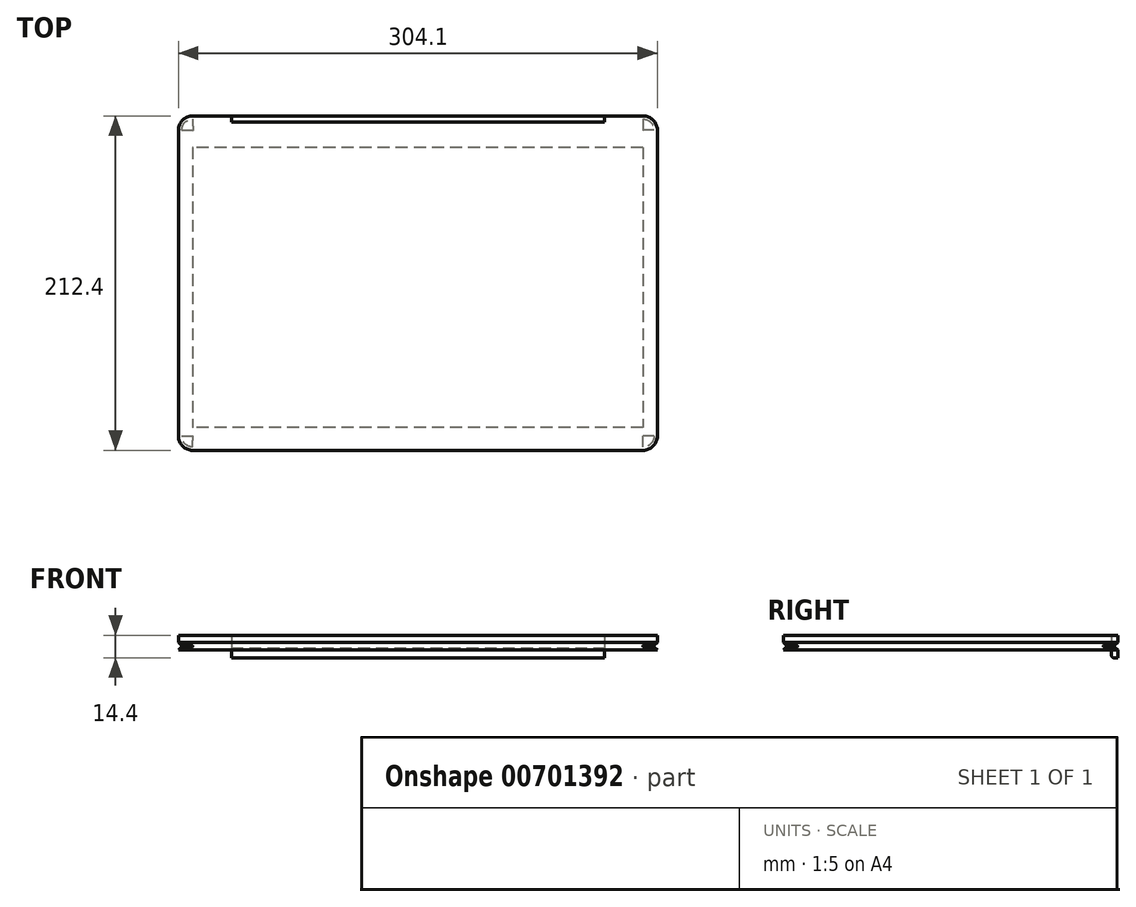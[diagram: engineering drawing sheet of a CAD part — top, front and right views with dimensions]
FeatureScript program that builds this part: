
annotation { "Feature Type Name" : "Feature", "Feature Type Description" : "" }
export const myFeature = defineFeature(function(context is Context, id is Id, definition is map)
    precondition{}
    {
        {
            assignVariable(context, id + "F0", {"name" : "swivel_depth", "anyValue" : 3 * mm});
        }
        {
            var Q0;
            Q0=qCreatedBy(makeId("Top.planeOp"),FACE);
            var sketch = newSketch(context, id + "F1", { "sketchPlane" : qUnion([Q0])});
            skLineSegment(sketch, "E0.bottom", {"start": v(143.05, -106.2) * mm, "end": v(-143.05, -106.2) * mm});
            skLineSegment(sketch, "E0.top", {"start": v(143.05, 106.2) * mm, "end": v(-143.05, 106.2) * mm});
            skLineSegment(sketch, "E0.left", {"start": v(152.05, -97.2) * mm, "end": v(152.05, 97.2) * mm});
            skLineSegment(sketch, "E0.right", {"start": v(-152.05, -97.2) * mm, "end": v(-152.05, 97.2) * mm});
            skPoint(sketch, "E0.middle", {"position": v(0, 0) * mm});
            skPoint(sketch, "E1.visualSharp", {"position": v(152.05, 106.2) * mm});
            skArc(sketch, "E1.filletArc", {"start": v(152.05, 97.2) * mm, "mid": v(149.41, 103.56) * mm, "end": v(143.05, 106.2) * mm});
            skPoint(sketch, "E2.visualSharp", {"position": v(-152.05, 106.2) * mm});
            skArc(sketch, "E2.filletArc", {"start": v(-143.05, 106.2) * mm, "mid": v(-149.41, 103.56) * mm, "end": v(-152.05, 97.2) * mm});
            skPoint(sketch, "E3.visualSharp", {"position": v(-152.05, -106.2) * mm});
            skArc(sketch, "E3.filletArc", {"start": v(-152.05, -97.2) * mm, "mid": v(-149.41, -103.56) * mm, "end": v(-143.05, -106.2) * mm});
            skPoint(sketch, "E4.visualSharp", {"position": v(152.05, -106.2) * mm});
            skArc(sketch, "E4.filletArc", {"start": v(143.05, -106.2) * mm, "mid": v(149.41, -103.56) * mm, "end": v(152.05, -97.2) * mm});
            skLineSegment(sketch, "E5", {"start": v(-118.5, 102.2) * mm, "end": v(118.5, 102.2) * mm});
            skPoint(sketch, "E6", {"position": v(0, 102.2) * mm});
            skPoint(sketch, "E7", {"position": v(0, 106.2) * mm});
            skLineSegment(sketch, "E8", {"start": v(-118.5, 102.2) * mm, "end": v(-118.5, 106.2) * mm});
            skLineSegment(sketch, "E9", {"start": v(118.5, 102.2) * mm, "end": v(118.5, 106.2) * mm});
            skSolve(sketch);
        }
        {
            var Q0;
            Q0=makeQuery(id+"F1.imprint","IMPRINT",FACE,{"disambiguationData":[TD([[makeQuery(id+"F1.imprint","IMPRINT",EDGE,{"derivedFrom":sQuery(id+"F1.wireOp",EDGE,"E0.bottom")}),-1.0]])]});
            var Q1;
            Q1=makeQuery(id+"F1.imprint","IMPRINT",FACE,{"disambiguationData":[TD([[makeQuery(id+"F1.imprint","IMPRINT",EDGE,{"derivedFrom":sQuery(id+"F1.wireOp",EDGE,"E5")}),1.0]])]});
            extrude(context, id + "F2", {"entities" : qUnion([Q0, Q1]), "depth" : 9.4 * mm, "offsetDistance" : 25 * mm});
        }
        {
            var Q0;
            Q0=makeQuery(id+"F2.opExtrude","CAP_FACE",FACE,{"disambiguationData":[OSD([sQuery(id+"F1.wireOp",EDGE,"E0.bottom"),sQuery(id+"F1.wireOp",EDGE,"E0.top"),sQuery(id+"F1.wireOp",EDGE,"E0.left"),sQuery(id+"F1.wireOp",EDGE,"E0.right"),sQuery(id+"F1.wireOp",EDGE,"E1.filletArc"),sQuery(id+"F1.wireOp",EDGE,"E2.filletArc"),sQuery(id+"F1.wireOp",EDGE,"E3.filletArc"),sQuery(id+"F1.wireOp",EDGE,"E4.filletArc"),sQuery(id+"F1.wireOp",EDGE,"E5"),sQuery(id+"F1.wireOp",EDGE,"E8"),sQuery(id+"F1.wireOp",EDGE,"E9")])],"isStart":true});
            chamfer(context, id + "F3", {"entities" : qUnion([Q0]), "width" : 5 * mm, "tangentPropagation" : true});
        }
        {
            var Q0;
            Q0=makeQuery(id+"F2.opExtrude","CAP_FACE",FACE,{"disambiguationData":[OSD([sQuery(id+"F1.wireOp",EDGE,"E0.bottom"),sQuery(id+"F1.wireOp",EDGE,"E0.top"),sQuery(id+"F1.wireOp",EDGE,"E0.left"),sQuery(id+"F1.wireOp",EDGE,"E0.right"),sQuery(id+"F1.wireOp",EDGE,"E1.filletArc"),sQuery(id+"F1.wireOp",EDGE,"E2.filletArc"),sQuery(id+"F1.wireOp",EDGE,"E3.filletArc"),sQuery(id+"F1.wireOp",EDGE,"E4.filletArc"),sQuery(id+"F1.wireOp",EDGE,"E5"),sQuery(id+"F1.wireOp",EDGE,"E8"),sQuery(id+"F1.wireOp",EDGE,"E9")])],"isStart":true});
            fillet(context, id + "F4", {"entities" : qUnion([Q0]), "radius" : 10 * mm, "tangentPropagation" : true, "allowEdgeOverflow" : false});
        }
        {
            var Q0;
            Q0=makeQuery(id+"F1.imprint","IMPRINT",FACE,{"disambiguationData":[TD([[makeQuery(id+"F1.imprint","IMPRINT",EDGE,{"derivedFrom":sQuery(id+"F1.wireOp",EDGE,"E5")}),1.0]])]});
            extrude(context, id + "F5", {"entities" : qUnion([Q0]), "operationType" : NewBodyOperationType.REMOVE, "depth" : 25 * mm, "offsetDistance" : 25 * mm});
        }
        {
            var Q0;
            Q0=makeQuery(id+"F1.imprint","IMPRINT",FACE,{"disambiguationData":[TD([[makeQuery(id+"F1.imprint","IMPRINT",EDGE,{"derivedFrom":sQuery(id+"F1.wireOp",EDGE,"E0.bottom")}),-1.0]])]});
            var Q1;
            Q1=makeQuery(id+"F1.imprint","IMPRINT",FACE,{"disambiguationData":[TD([[makeQuery(id+"F1.imprint","IMPRINT",EDGE,{"derivedFrom":sQuery(id+"F1.wireOp",EDGE,"E5")}),1.0]])]});
            extrude(context, id + "F6", {"entities" : qUnion([Q0, Q1]), "depth" : 5 * mm, "offsetDistance" : 25 * mm});
        }
        {
            var Q0;
            Q0=makeQuery(id+"F1.imprint","IMPRINT",FACE,{"disambiguationData":[TD([[makeQuery(id+"F1.imprint","IMPRINT",EDGE,{"derivedFrom":sQuery(id+"F1.wireOp",EDGE,"E0.bottom")}),-1.0]])]});
            var sketch = newSketch(context, id + "F7", { "sketchPlane" : qUnion([Q0])});
            skLineSegment(sketch, "E10.bottom", {"start": v(143.05, 86.2) * mm, "end": v(-143.05, 86.2) * mm});
            skLineSegment(sketch, "E10.top", {"start": v(143.05, -91.8) * mm, "end": v(-143.05, -91.8) * mm});
            skLineSegment(sketch, "E10.left", {"start": v(143.05, 86.2) * mm, "end": v(143.05, -91.8) * mm});
            skLineSegment(sketch, "E10.right", {"start": v(-143.05, 86.2) * mm, "end": v(-143.05, -91.8) * mm});
            skPoint(sketch, "E10.middle", {"position": v(0, -2.8) * mm});
            skSolve(sketch);
        }
        {
            var Q0;
            Q0=makeQuery(id+"F7.imprint","IMPRINT",FACE,{"disambiguationData":[TD([[makeQuery(id+"F7.imprint","IMPRINT",EDGE,{"derivedFrom":sQuery(id+"F7.wireOp",EDGE,"E10.bottom")}),1.0]])]});
            extrude(context, id + "F8", {"entities" : qUnion([Q0]), "operationType" : NewBodyOperationType.REMOVE, "depth" : .25 * mm, "offsetDistance" : 25 * mm});
        }
        {
            var Q0;
            Q0=makeQuery(id+"F1.imprint","IMPRINT",FACE,{"disambiguationData":[TD([[makeQuery(id+"F1.imprint","IMPRINT",EDGE,{"derivedFrom":sQuery(id+"F1.wireOp",EDGE,"E5")}),1.0]])]});
            extrude(context, id + "F9", {"entities" : qUnion([Q0]), "operationType" : NewBodyOperationType.ADD, "oppositeDirection" : true, "depth" : getVariable(context, 'swivel_depth'), "offsetDistance" : 25 * mm});
        }
        {
            var Q0;
            Q0=makeQuery(id+"F9.opExtrude","SWEPT_FACE",FACE,{"disambiguationData":[OSD([sQuery(id+"F1.wireOp",EDGE,"E8")])]});
            var sketch = newSketch(context, id + "F10", { "sketchPlane" : qUnion([Q0])});
            skCircle(sketch, "E11", {"center": v(-104.2, -3) * mm, "radius": 2 * mm});
            skLineSegment(sketch, "E12", {"start": v(-106.2, -3) * mm, "end": v(-106.2, -5) * mm});
            skLineSegment(sketch, "E13", {"start": v(-106.2, -5) * mm, "end": v(-104.2, -5) * mm});
            skSolve(sketch);
        }
        {
            var Q0;
            {var subQ1=sQuery(id+"F1.wireOp",EDGE,"E8");var subQ2=makeQuery(id+"F9.opExtrude","CAP_EDGE",EDGE,{"disambiguationData":[OSD([subQ1])],"isStart":false});Q0=makeQuery(id+"F10.imprint","IMPRINT",FACE,{"disambiguationData":[TD([[makeQuery(id+"F10.imprint","IMPRINT",EDGE,{"derivedFrom":subQ2}),1.0]])]});}
            var Q1;
            {var subQ0=sQuery(id+"F10.wireOp",EDGE,"E12");Q1=makeQuery(id+"F10.imprint","IMPRINT",FACE,{"disambiguationData":[TD([[makeQuery(id+"F10.imprint","IMPRINT",EDGE,{"derivedFrom":subQ0}),1.0]])]});}
            extrude(context, id + "F11", {"entities" : qUnion([Q0, Q1]), "operationType" : NewBodyOperationType.ADD, "oppositeDirection" : true, "depth" : 237 * mm, "offsetDistance" : 25 * mm});
        }
        {
            var Q0;
            Q0=makeQuery(id+"F6.opExtrude","CAP_FACE",FACE,{"disambiguationData":[OSD([sQuery(id+"F1.wireOp",EDGE,"E0.bottom"),sQuery(id+"F1.wireOp",EDGE,"E0.top"),sQuery(id+"F1.wireOp",EDGE,"E0.left"),sQuery(id+"F1.wireOp",EDGE,"E0.right"),sQuery(id+"F1.wireOp",EDGE,"E1.filletArc"),sQuery(id+"F1.wireOp",EDGE,"E2.filletArc"),sQuery(id+"F1.wireOp",EDGE,"E3.filletArc"),sQuery(id+"F1.wireOp",EDGE,"E4.filletArc")])],"isStart":false});
            chamfer(context, id + "F12", {"entities" : qUnion([Q0]), "width" : 5 * mm, "tangentPropagation" : true});
        }
        {
            var Q0;
            Q0=makeQuery(id+"F6.opExtrude","CAP_FACE",FACE,{"disambiguationData":[OSD([sQuery(id+"F1.wireOp",EDGE,"E0.bottom"),sQuery(id+"F1.wireOp",EDGE,"E0.top"),sQuery(id+"F1.wireOp",EDGE,"E0.left"),sQuery(id+"F1.wireOp",EDGE,"E0.right"),sQuery(id+"F1.wireOp",EDGE,"E1.filletArc"),sQuery(id+"F1.wireOp",EDGE,"E2.filletArc"),sQuery(id+"F1.wireOp",EDGE,"E3.filletArc"),sQuery(id+"F1.wireOp",EDGE,"E4.filletArc")])],"isStart":false});
            fillet(context, id + "F13", {"entities" : qUnion([Q0]), "radius" : 10 * mm, "tangentPropagation" : true, "allowEdgeOverflow" : false});
        }
    });
